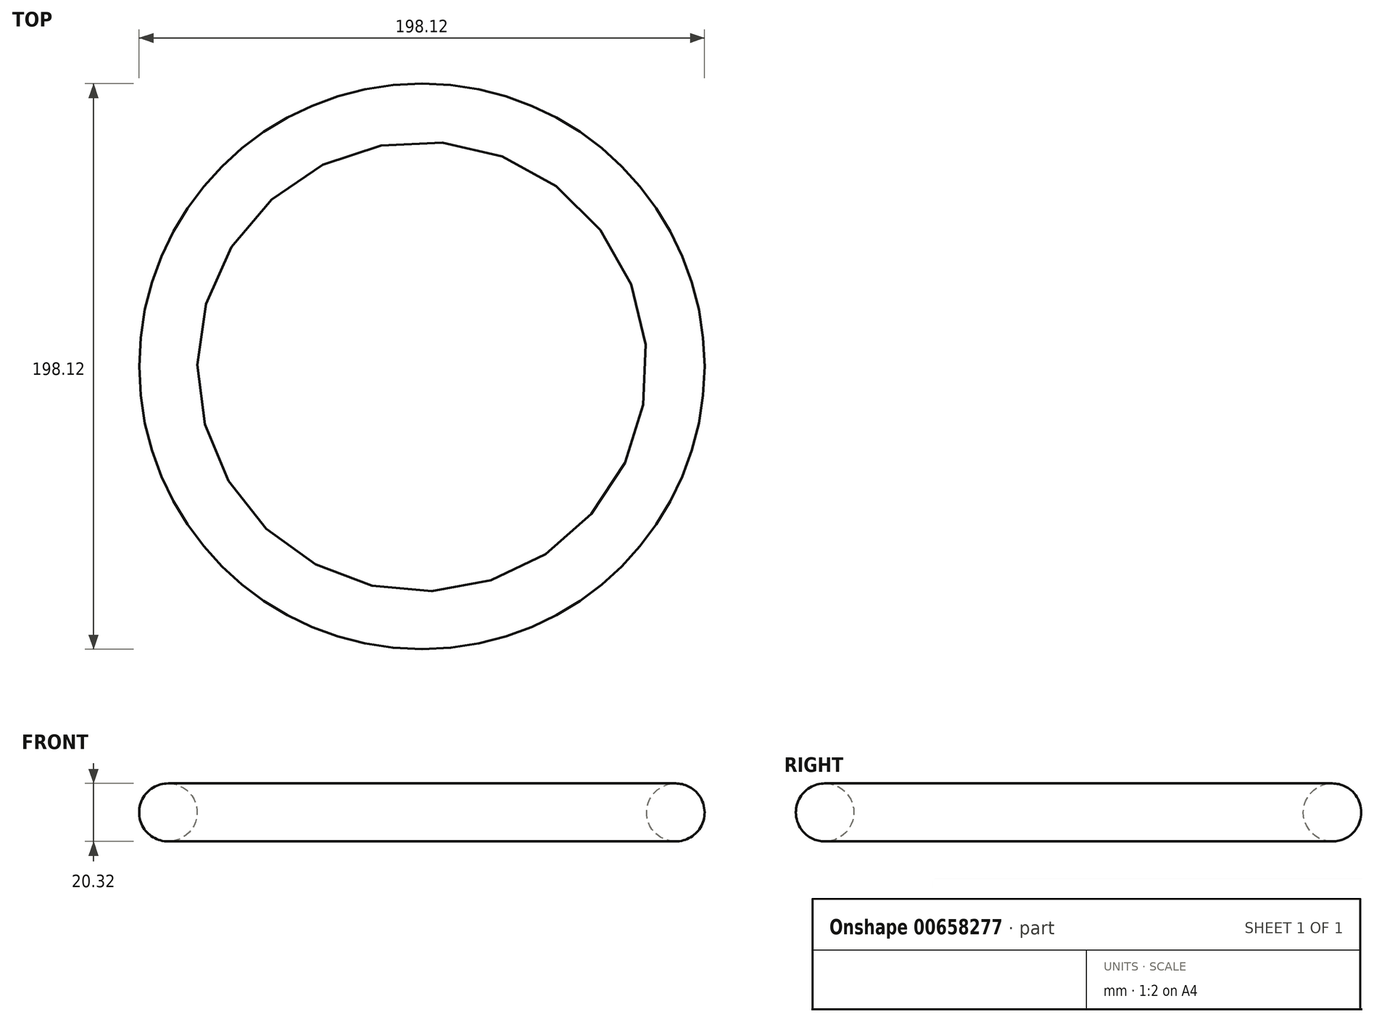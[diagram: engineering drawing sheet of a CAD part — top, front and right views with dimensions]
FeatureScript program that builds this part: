
annotation { "Feature Type Name" : "Feature", "Feature Type Description" : "" }
export const myFeature = defineFeature(function(context is Context, id is Id, definition is map)
    precondition{}
    {
        {
            var Q0;
            Q0=qCreatedBy(makeId("Front.planeOp"),FACE);
            var sketch = newSketch(context, id + "F0", { "sketchPlane" : qUnion([Q0])});
            skCircle(sketch, "E0", {"center": v(0, 0) * mm, "radius": 10.16 * mm});
            skSolve(sketch);
        }
        {
            var Q0;
            Q0=qCreatedBy(makeId("Top.planeOp"),FACE);
            var sketch = newSketch(context, id + "F1", { "sketchPlane" : qUnion([Q0])});
            skCircle(sketch, "E1", {"center": v(-88.9, 0.65) * mm, "radius": 88.9 * mm});
            skPoint(sketch, "E1.first.point", {"position": v(0, 0) * mm});
            skPoint(sketch, "E1.second.point", {"position": v(-177.8, 0) * mm});
            skPoint(sketch, "E1.third.point", {"position": v(-82.37, -88) * mm});
            skSolve(sketch);
        }
        {
            var Q0;
            Q0=makeQuery(id+"F0.imprint","IMPRINT",FACE,{"disambiguationData":[TD([[makeQuery(id+"F0.imprint","IMPRINT",EDGE,{"derivedFrom":sQuery(id+"F0.wireOp",EDGE,"E0")}),1.0]])]});
            var Q1;
            Q1=sQuery(id+"F1.wireOp",EDGE,"E1");
            sweep(context, id + "F2", {"profiles" : qUnion([Q0]), "path" : qUnion([Q1])});
        }
    });
